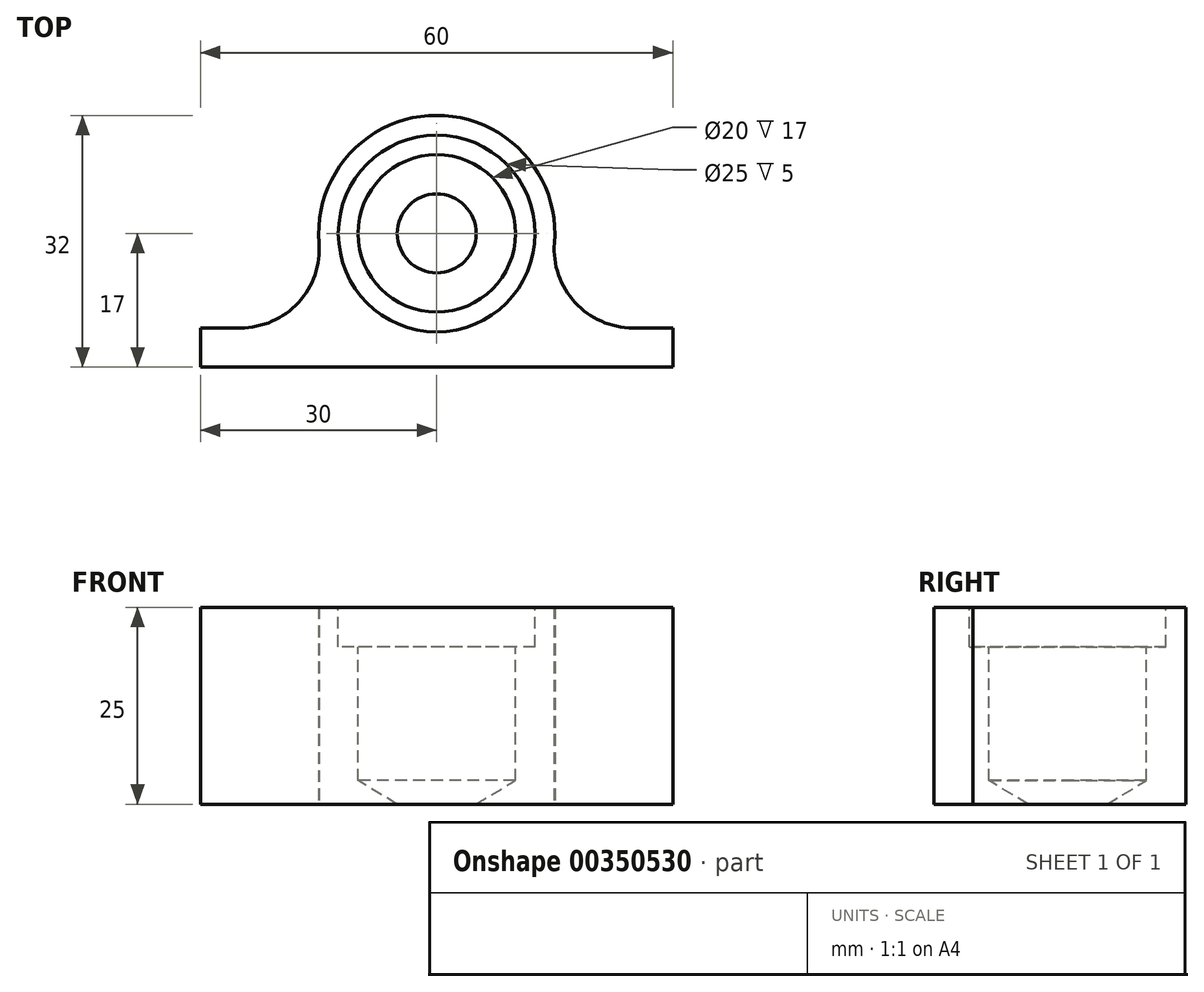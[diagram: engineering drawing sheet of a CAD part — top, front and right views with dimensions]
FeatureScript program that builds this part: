
annotation { "Feature Type Name" : "Feature", "Feature Type Description" : "" }
export const myFeature = defineFeature(function(context is Context, id is Id, definition is map)
    precondition{}
    {
        {
            var Q0;
            Q0=qCreatedBy(makeId("Top.planeOp"),FACE);
            var sketch = newSketch(context, id + "F0", { "sketchPlane" : qUnion([Q0])});
            skCircle(sketch, "E0", {"center": v(0, 0) * mm, "radius": 15 * mm});
            skLineSegment(sketch, "E1.bottom", {"start": v(30, -12) * mm, "end": v(-30, -12) * mm});
            skLineSegment(sketch, "E1.top", {"start": v(30, -17) * mm, "end": v(-30, -17) * mm});
            skLineSegment(sketch, "E1.left", {"start": v(30, -12) * mm, "end": v(30, -17) * mm});
            skLineSegment(sketch, "E1.right", {"start": v(-30, -12) * mm, "end": v(-30, -17) * mm});
            skPoint(sketch, "E1.middle", {"position": v(0, -14.5) * mm});
            skSolve(sketch);
        }
        {
            var Q0;
            {var subQ0=sQuery(id+"F0.wireOp",EDGE,"E1.bottom");var subQ1=sQuery(id+"F0.wireOp",EDGE,"E0");var subQ2=makeQuery(id+"F0.imprint","INTERSECT",VERTEX,{"disambiguationData":[OD(0.0)],"derivedFrom":[subQ1,subQ0]});Q0=makeQuery(id+"F0.imprint","IMPRINT",FACE,{"disambiguationData":[TD([[makeQuery(id+"F0.imprint","IMPRINT",EDGE,{"disambiguationData":[TD([[subQ2,-1.0]])],"derivedFrom":subQ1}),1.0]])]});}
            var Q1;
            Q1=makeQuery(id+"F0.imprint","IMPRINT",FACE,{"disambiguationData":[TD([[makeQuery(id+"F0.imprint","IMPRINT",EDGE,{"derivedFrom":sQuery(id+"F0.wireOp",EDGE,"E1.top")}),-1.0]])]});
            var Q2;
            {var subQ0=sQuery(id+"F0.wireOp",EDGE,"E1.bottom");var subQ1=sQuery(id+"F0.wireOp",EDGE,"E0");var subQ2=makeQuery(id+"F0.imprint","INTERSECT",VERTEX,{"disambiguationData":[OD(0.0)],"derivedFrom":[subQ1,subQ0]});Q2=makeQuery(id+"F0.imprint","IMPRINT",FACE,{"disambiguationData":[TD([[makeQuery(id+"F0.imprint","IMPRINT",EDGE,{"disambiguationData":[TD([[subQ2,1.0]])],"derivedFrom":subQ1}),1.0]])]});}
            extrude(context, id + "F1", {"entities" : qUnion([Q0, Q1, Q2]), "depth" : 25 * mm});
        }
        {
            var Q0;
            {var subQ0=sQuery(id+"F0.wireOp",EDGE,"E1.bottom");var subQ1=sQuery(id+"F0.wireOp",EDGE,"E0");Q0=makeQuery(id+"F1.opExtrude","SWEPT_EDGE",EDGE,{"disambiguationData":[OSD([subQ1,subQ0]),TDD([makeQuery(id+"F0.imprint","INTERSECT",VERTEX,{"disambiguationData":[OD(0.0)],"derivedFrom":[subQ1,subQ0]})])]});}
            var Q1;
            {var subQ0=sQuery(id+"F0.wireOp",EDGE,"E1.bottom");var subQ1=sQuery(id+"F0.wireOp",EDGE,"E0");Q1=makeQuery(id+"F1.opExtrude","SWEPT_EDGE",EDGE,{"disambiguationData":[OSD([subQ1,subQ0]),TDD([makeQuery(id+"F0.imprint","INTERSECT",VERTEX,{"disambiguationData":[OD(1.0)],"derivedFrom":[subQ1,subQ0]})])]});}
            fillet(context, id + "F2", {"entities" : qUnion([Q0, Q1]), "radius" : 10 * mm, "tangentPropagation" : true, "allowEdgeOverflow" : false});
        }
        {
            var Q0;
            Q0=makeQuery(id+"F1.opExtrude","CAP_FACE",FACE,{"disambiguationData":[OSD([sQuery(id+"F0.wireOp",EDGE,"E0"),sQuery(id+"F0.wireOp",EDGE,"E1.bottom"),sQuery(id+"F0.wireOp",EDGE,"E1.top"),sQuery(id+"F0.wireOp",EDGE,"E1.left"),sQuery(id+"F0.wireOp",EDGE,"E1.right")])],"isStart":false});
            var sketch = newSketch(context, id + "F3", { "sketchPlane" : qUnion([Q0])});
            skPoint(sketch, "E2", {"position": v(0, 0) * mm});
            skSolve(sketch);
        }
        {
            var Q0;
            Q0=sQuery(id+"F3.wireOp",VERTEX,"E2");
            var Q1;
            Q1=makeQuery(id+"F1.opExtrude","SWEPT_BODY",BODY,{"disambiguationData":[OSD([sQuery(id+"F0.wireOp",EDGE,"E0"),sQuery(id+"F0.wireOp",EDGE,"E1.bottom"),sQuery(id+"F0.wireOp",EDGE,"E1.top"),sQuery(id+"F0.wireOp",EDGE,"E1.left"),sQuery(id+"F0.wireOp",EDGE,"E1.right")])]});
            hole(context, id + "F4", {"style" : HoleStyle.C_BORE, "endStyle" : HoleEndStyle.BLIND, "holeDiameter" : 20 * mm, "cBoreDiameter" : 25 * mm, "cBoreDepth" : 5 * mm, "holeDepth" : 22 * mm, "isTappedThrough" : true, "tappedDepth" : 12 * mm, "tapClearance" : 3, "locations" : qUnion([Q0]), "scope" : qUnion([Q1])});
        }
    });
